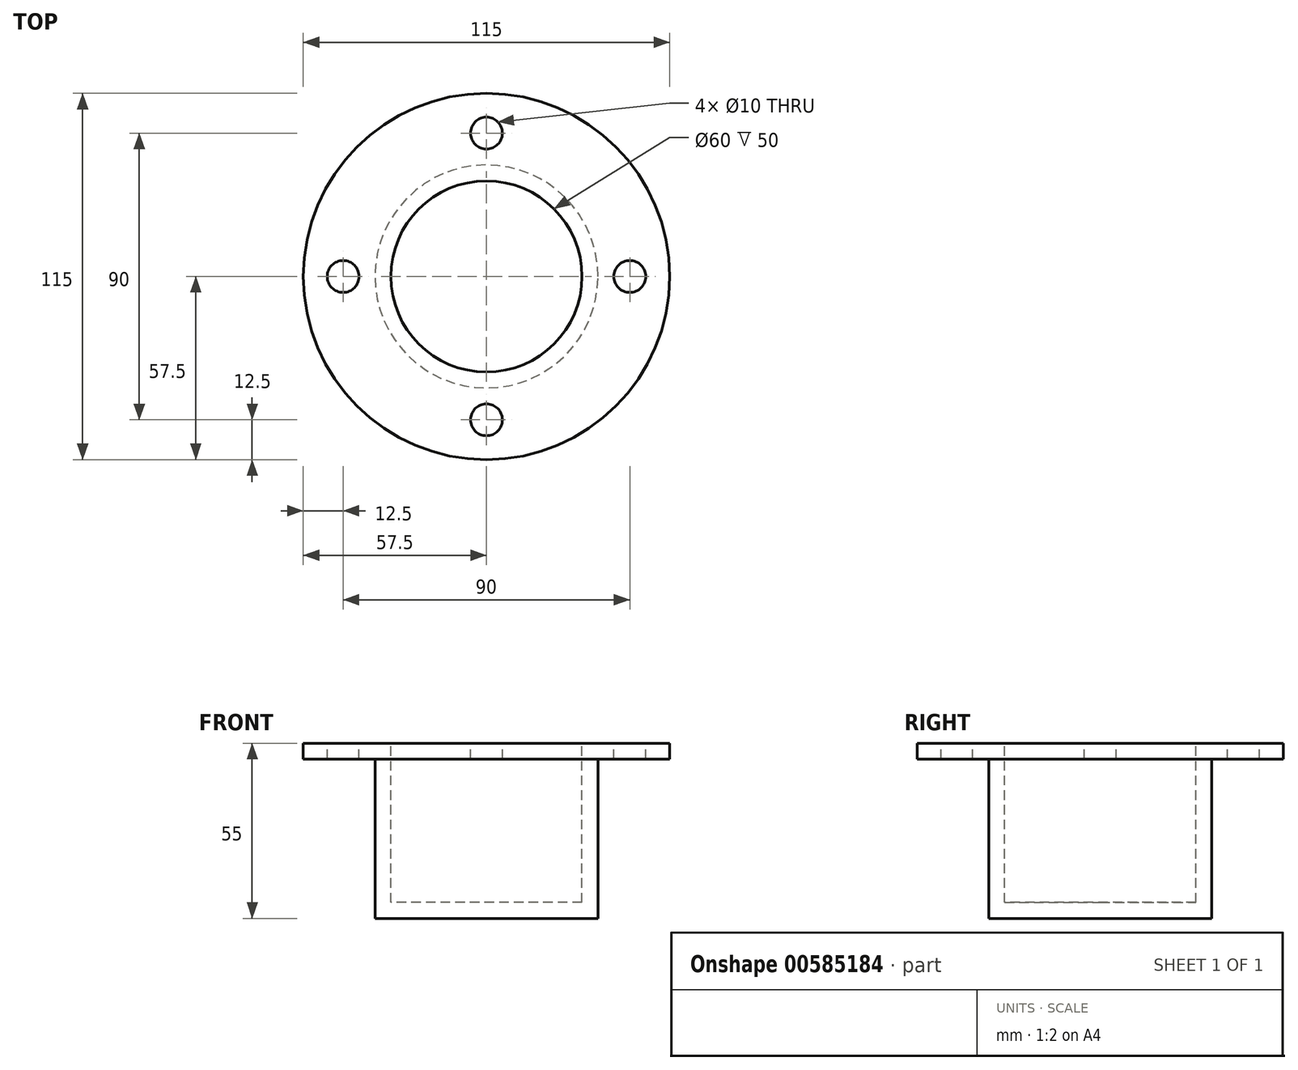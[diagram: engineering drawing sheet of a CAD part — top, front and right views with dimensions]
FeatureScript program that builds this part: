
annotation { "Feature Type Name" : "Feature", "Feature Type Description" : "" }
export const myFeature = defineFeature(function(context is Context, id is Id, definition is map)
    precondition{}
    {
        {
            var Q0;
            Q0=qCreatedBy(makeId("Front.planeOp"),FACE);
            var sketch = newSketch(context, id + "F0", { "sketchPlane" : qUnion([Q0])});
            skLineSegment(sketch, "E0", {"start": v(-57.5, 50) * mm, "end": v(-30, 50) * mm});
            skLineSegment(sketch, "E1", {"start": v(-30, 50) * mm, "end": v(-30, 0) * mm});
            skLineSegment(sketch, "E2", {"start": v(-30, 0) * mm, "end": v(0, 0) * mm});
            skLineSegment(sketch, "E3", {"start": v(0, -5) * mm, "end": v(-35, -5) * mm});
            skLineSegment(sketch, "E4", {"start": v(-35, -5) * mm, "end": v(-35, 45) * mm});
            skLineSegment(sketch, "E5", {"start": v(-35, 45) * mm, "end": v(-57.5, 45) * mm});
            skLineSegment(sketch, "E6", {"start": v(-57.5, 45) * mm, "end": v(-57.5, 50) * mm});
            skLineSegment(sketch, "E7", {"start": v(0, 104.35) * mm, "end": v(0, -64.35) * mm, "construction": true});
            skLineSegment(sketch, "E8", {"start": v(0, 0) * mm, "end": v(0, -5) * mm});
            skSolve(sketch);
        }
        {
            var Q0;
            Q0 = qSketchRegion(id + "F0", true);
            var Q1;
            Q1=sQuery(id+"F0.wireOp",EDGE,"E7");
            revolve(context, id + "F1", {"entities" : qUnion([Q0]), "axis" : qUnion([Q1]), "revolveType" : RevolveType.FULL});
        }
        {
            var Q0;
            Q0=makeQuery(id+"F1.opRevolve","SWEPT_FACE",FACE,{"disambiguationData":[OSD([sQuery(id+"F0.wireOp",EDGE,"E0")])]});
            var sketch = newSketch(context, id + "F2", { "sketchPlane" : qUnion([Q0])});
            skPoint(sketch, "E9", {"position": v(0, 0) * mm});
            skCircle(sketch, "E10", {"center": v(0, 45) * mm, "radius": 5 * mm});
            skCircle(sketch, "E11.1.0", {"center": v(-45, 0) * mm, "radius": 5 * mm});
            skCircle(sketch, "E11.2.0", {"center": v(0, -45) * mm, "radius": 5 * mm});
            skCircle(sketch, "E11.3.0", {"center": v(45, 0) * mm, "radius": 5 * mm});
            skSolve(sketch);
        }
        {
            var Q0;
            Q0 = qSketchRegion(id + "F2", true);
            extrude(context, id + "F3", {"entities" : qUnion([Q0]), "operationType" : NewBodyOperationType.REMOVE, "oppositeDirection" : true, "depth" : 25 * mm, "offsetDistance" : 25 * mm});
        }
    });
